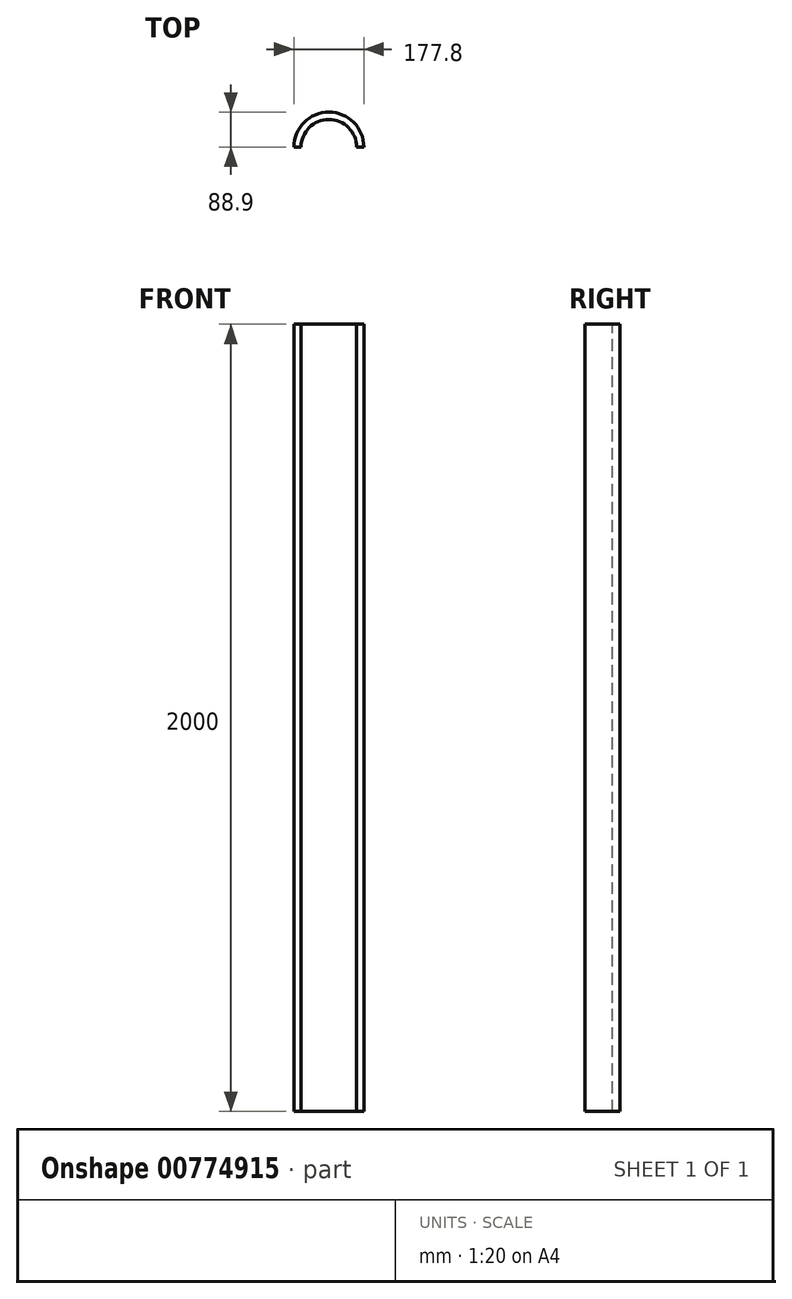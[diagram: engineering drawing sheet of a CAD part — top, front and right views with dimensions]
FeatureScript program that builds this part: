
annotation { "Feature Type Name" : "Feature", "Feature Type Description" : "" }
export const myFeature = defineFeature(function(context is Context, id is Id, definition is map)
    precondition{}
    {
        {
            var Q0;
            Q0=qCreatedBy(makeId("Top.planeOp"),FACE);
            var sketch = newSketch(context, id + "F0", { "sketchPlane" : qUnion([Q0])});
            skArc(sketch, "E0", {"start": v(88.9, 0) * mm, "mid": v(0, 88.9) * mm, "end": v(-88.9, 0) * mm});
            skArc(sketch, "E1", {"start": v(70.5, 0) * mm, "mid": v(0, 70.5) * mm, "end": v(-70.5, 0) * mm});
            skLineSegment(sketch, "E2", {"start": v(0, 0) * mm, "end": v(-88.9, 0) * mm, "construction": true});
            skLineSegment(sketch, "E3", {"start": v(-88.9, 0) * mm, "end": v(0, 0) * mm, "construction": true});
            skLineSegment(sketch, "E4", {"start": v(88.9, 0) * mm, "end": v(0, 0) * mm, "construction": true});
            skLineSegment(sketch, "E5", {"start": v(-70.5, 0) * mm, "end": v(-88.9, 0) * mm});
            skLineSegment(sketch, "E6", {"start": v(70.5, 0) * mm, "end": v(88.9, 0) * mm});
            skSolve(sketch);
        }
        {
            var Q0;
            Q0=makeQuery(id+"F0.imprint","IMPRINT",FACE,{"disambiguationData":[TD([[makeQuery(id+"F0.imprint","IMPRINT",EDGE,{"derivedFrom":sQuery(id+"F0.wireOp",EDGE,"E0")}),1.0]])]});
            extrude(context, id + "F1", {"entities" : qUnion([Q0]), "oppositeDirection" : true, "depth" : 2000 * mm, "offsetDistance" : 25 * mm});
        }
    });
